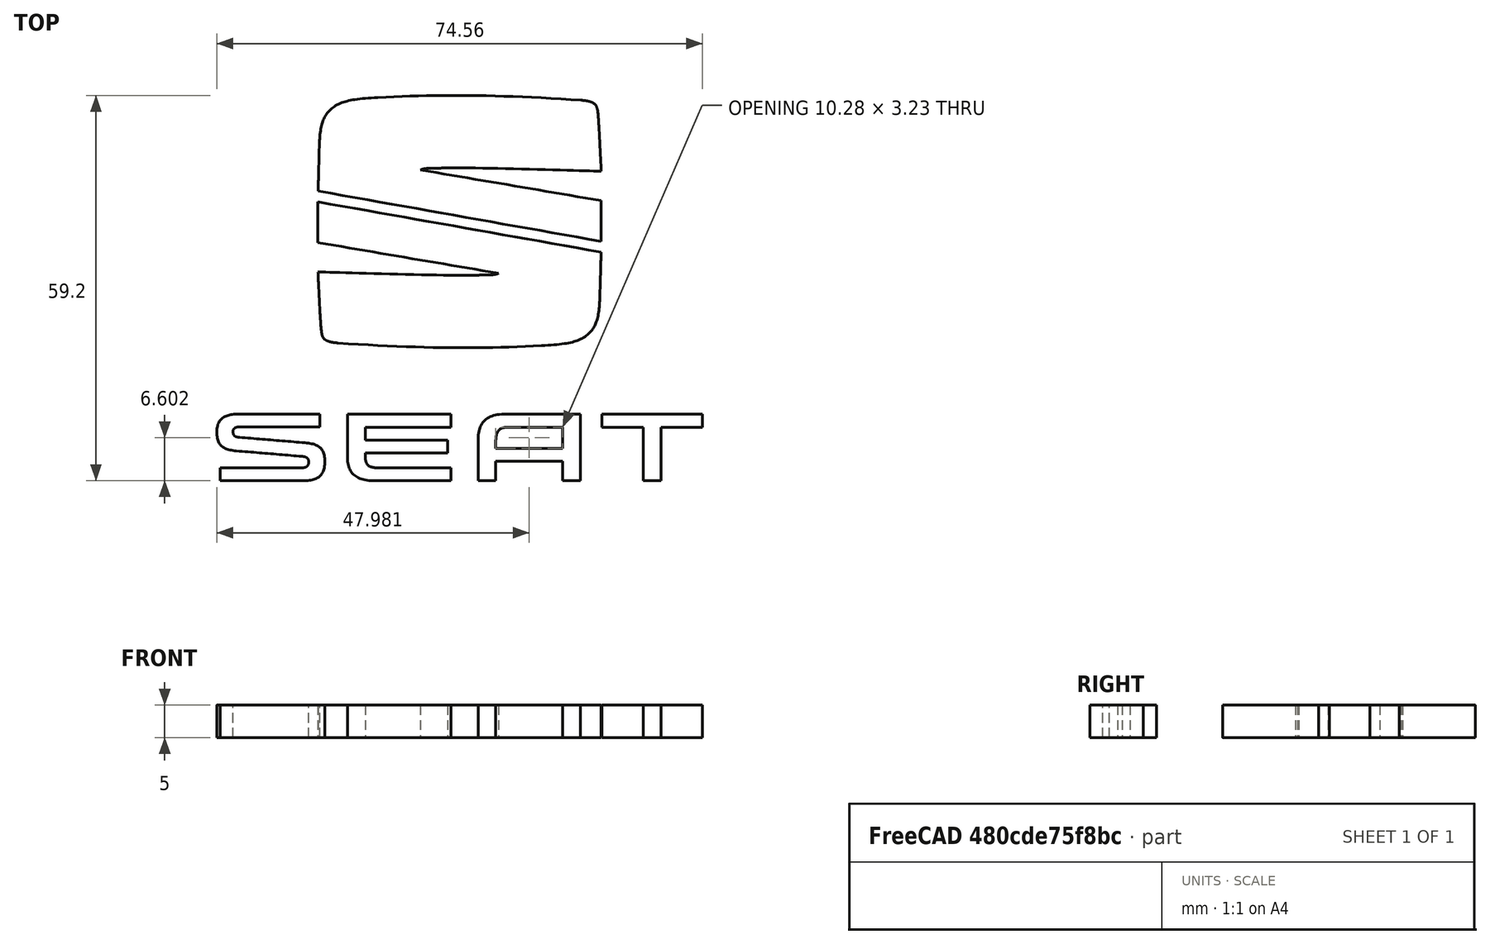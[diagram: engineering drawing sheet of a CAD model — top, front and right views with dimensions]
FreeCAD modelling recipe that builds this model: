
FCSTD DOCUMENT  (FreeCAD 0.17R10893 (Git))
Label: SEAT2000
License: CreativeCommons Attribution-ShareAlike
LicenseURL: http://creativecommons.org/licenses/by-sa/4.0/
objects: Part::Feature×7, Part::Extrusion×7, Path::FeaturePython×7, Sketcher::SketchObject×1, PartDesign::Body×1, Part::Cut×1, Part::MultiFuse×1, Path::FeatureCompoundPython×1
note: 18 computed .brp shape members not serialized (recipe doc carries the construction recipe); baked Part::Feature solids carry a one-line shape summary decoded from their .brp

FEATURE [Part::Feature] path3013
  shape: bbox 16.59 x 10.22 x 2.5e-07 mm, 0 faces, 0 solids (baked)
FEATURE [Part::Feature] path3013001
  shape: bbox 15.87 x 10.22 x 2.5e-07 mm, 0 faces, 0 solids (baked)
FEATURE [Part::Feature] path3013002
  shape: bbox 15.42 x 10.22 x 2.5e-07 mm, 0 faces, 0 solids (baked)
FEATURE [Part::Feature] path3013003
  shape: bbox 15.7 x 10.22 x 2.5e-07 mm, 0 faces, 0 solids (baked)
FEATURE [Part::Feature] path3013004
  shape: bbox 10.28 x 3.233 x 2.5e-07 mm, 0 faces, 0 solids (baked)
FEATURE [Part::Feature] path3017
  shape: bbox 43.47 x 22.61 x 2.5e-07 mm, 0 faces, 0 solids (baked)
FEATURE [Part::Feature] path3021
  shape: bbox 43.47 x 22.61 x 2.5e-07 mm, 0 faces, 0 solids (baked)
FEATURE [Sketcher::SketchObject] Sketch
  MapMode = 5
  Support = -> [XY_Plane]
FEATURE [PartDesign::Body] Body
  Group = -> [Sketch]
  Origin = -> BodyOrigin
FEATURE [Part::Extrusion] Extrude
  Base = -> path3017
  Dir = (0,0,-1)
  DirMode = 2
  FaceMakerClass = Part::FaceMakerBullseye
  LengthFwd = 5
  LengthRev = 0
  Placement = pos=(0,0,5) rot=(0,0,1;0rad)
  Solid = true
  Symmetric = false
FEATURE [Part::Extrusion] Extrude001
  Base = -> path3021
  Dir = (0,0,-1)
  DirMode = 2
  FaceMakerClass = Part::FaceMakerBullseye
  LengthFwd = 5
  LengthRev = 0
  Placement = pos=(0,0,5) rot=(0,0,1;0rad)
  Solid = true
  Symmetric = false
FEATURE [Part::Extrusion] Extrude002
  Base = -> path3013
  Dir = (0,0,1)
  DirMode = 2
  FaceMakerClass = Part::FaceMakerBullseye
  LengthFwd = 5
  LengthRev = 0
  Solid = true
  Symmetric = false
FEATURE [Part::Extrusion] Extrude003
  Base = -> path3013001
  Dir = (0,0,-1)
  DirMode = 2
  FaceMakerClass = Part::FaceMakerBullseye
  LengthFwd = 5
  LengthRev = 0
  Placement = pos=(0,0,5) rot=(0,0,1;0rad)
  Solid = true
  Symmetric = false
FEATURE [Part::Extrusion] Extrude004
  Base = -> path3013003
  Dir = (0,0,1)
  DirMode = 2
  FaceMakerClass = Part::FaceMakerBullseye
  LengthFwd = 5
  LengthRev = 0
  Solid = true
  Symmetric = false
FEATURE [Part::Extrusion] Extrude005
  Base = -> path3013002
  Dir = (0,0,1)
  DirMode = 2
  FaceMakerClass = Part::FaceMakerBullseye
  LengthFwd = 5
  LengthRev = 0
  Solid = true
  Symmetric = false
FEATURE [Part::Extrusion] Extrude006
  Base = -> path3013004
  Dir = (0,0,-1)
  DirMode = 2
  FaceMakerClass = Part::FaceMakerBullseye
  LengthFwd = 10
  LengthRev = 0
  Placement = pos=(0,0,7) rot=(0,0,1;0rad)
  Solid = true
  Symmetric = false
FEATURE [Part::Cut] Cut
  Base = -> Extrude004
  Tool = -> Extrude006
FEATURE [Part::MultiFuse] Fusion  label="seat"
  Shapes = -> [Extrude,Extrude001,Extrude002,Extrude003,Extrude005,Cut]
FEATURE [Path::FeaturePython] Default_Tool  # Path/CAM operation (typed FeaturePython)
  HorizFeed = 200
  HorizRapid = 200
  SpindleDir = 0
  SpindleSpeed = 0
  ToolNumber = 1
  VertFeed = 200
  VertRapid = 200
FEATURE [Path::FeaturePython] Contour  # Path/CAM operation (typed FeaturePython)
  Active = true
  ClearanceHeight = 8
  Direction = 0
  EndPoint = (0,0,0)
  ExtendAtEnd = 0
  ExtendAtStart = 0
  FinalDepth = 0
  LeadInLineLen = 0
  LeadOutLineLen = 0
  OffsetExtra = 0
  RollRadius = 0
  SafeHeight = 8
  Side = 0
  StartDepth = 5
  StartPoint = (0,0,0)
  StepDown = 1
  ToolController = -> Default_Tool
  UseComp = true
  UseEndPoint = false
  UseStartPoint = false
FEATURE [Path::FeaturePython] Profile  # Path/CAM operation (typed FeaturePython)
  Active = true
  Base = -> [Fusion]
  ClearanceHeight = 8
  Direction = 0
  EndPoint = (0,0,0)
  ExtendAtEnd = 0
  ExtendAtStart = 0
  FinalDepth = 0
  LeadInLineLen = 0
  LeadOutLineLen = 0
  OffsetExtra = 0
  RollRadius = 0
  SafeHeight = 8
  Side = 0
  StartDepth = 5
  StartPoint = (0,0,0)
  StepDown = 1
  ToolController = -> Default_Tool
  UseComp = true
  UseEndPoint = false
  UseStartPoint = false
  processCircles = true
  processHoles = true
  processPerimeter = true
FEATURE [Path::FeaturePython] Profile001 .. Profile004  x4 (patterned run collapsed; names and placements below)
  Active = true
  Base = -> [Fusion]
  ClearanceHeight = 10
  Direction = 0
  EndPoint = (0,0,0)
  ExtendAtEnd = 0
  ExtendAtStart = 0
  FinalDepth = 0
  LeadInLineLen = 0
  LeadOutLineLen = 0
  OffsetExtra = 0
  RollRadius = 0
  SafeHeight = 8
  Side = 0
  StartDepth = 5
  StartPoint = (0,0,0)
  StepDown = 1
  ToolController = -> Default_Tool
  UseComp = true
  UseEndPoint = false
  UseStartPoint = false
  processCircles = false
  processHoles = false
  processPerimeter = true
FEATURE [Path::FeatureCompoundPython] Job  # Path/CAM operation (typed FeaturePython)
  Base = -> Fusion
  GeometryTolerance = 0.01
  Group = -> [Default_Tool,Contour,Profile,Profile001,Profile002,Profile003,Profile004]
  MachineName = BigMill
  MachineUnits = 0
  PostProcessor = 0
  UsePlacements = false
  X_Max = 609.6
  X_Min = -609.6
  Y_Max = 152.4
  Y_Min = -152.4
  Z_Max = 304.8
  Z_Min = 0
